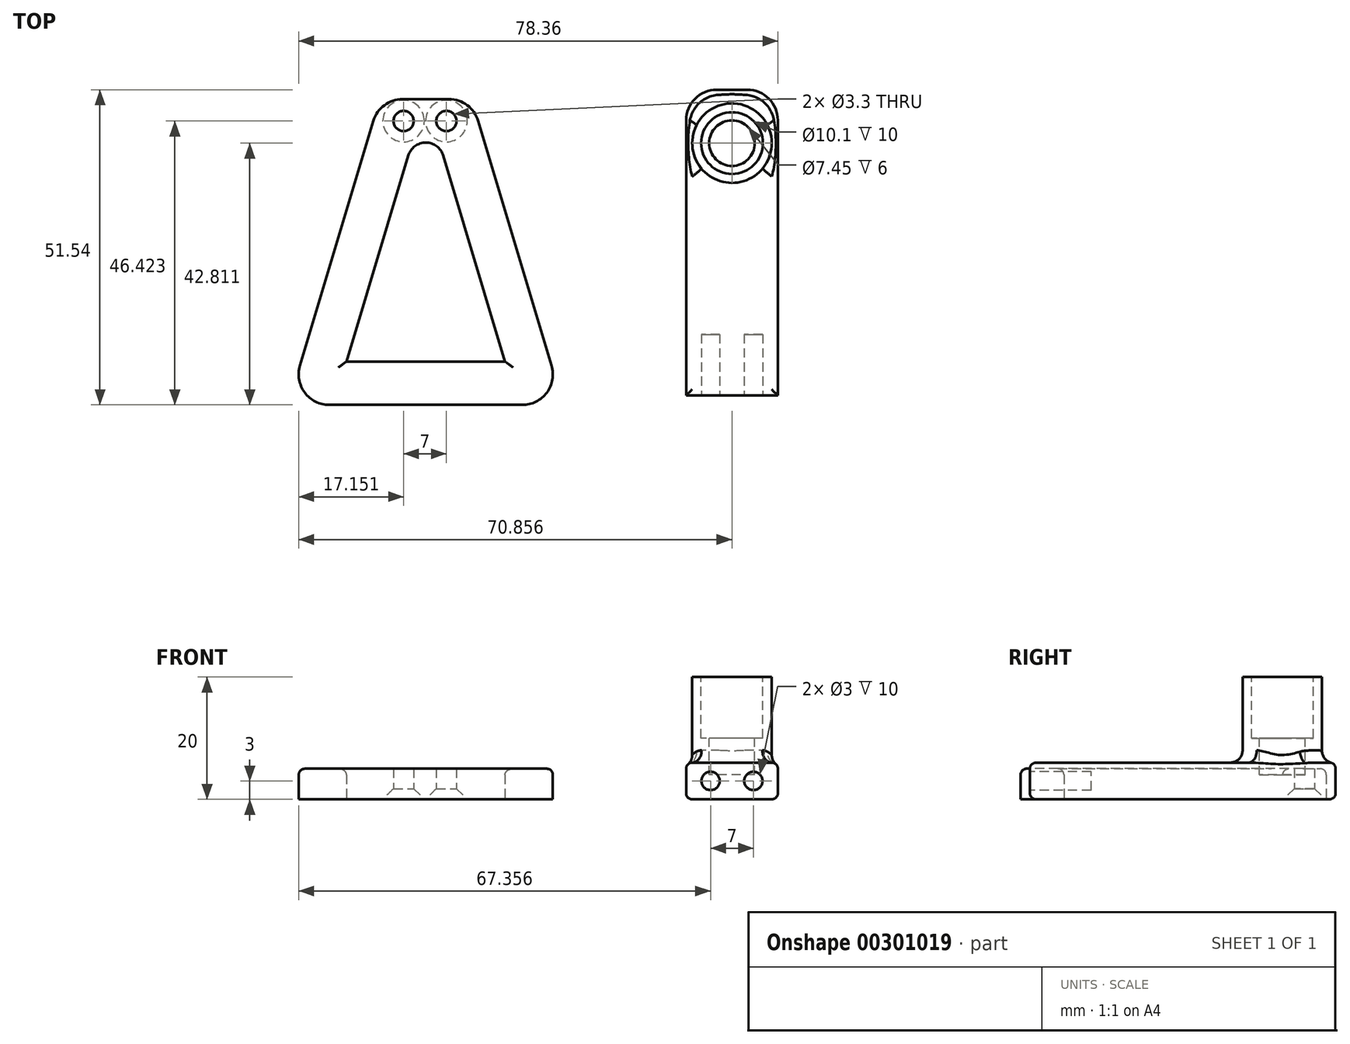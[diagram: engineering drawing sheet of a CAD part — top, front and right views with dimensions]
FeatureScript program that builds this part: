
annotation { "Feature Type Name" : "Feature", "Feature Type Description" : "" }
export const myFeature = defineFeature(function(context is Context, id is Id, definition is map)
    precondition{}
    {
        {
            var Q0;
            Q0=qCreatedBy(makeId("Top.planeOp"),FACE);
            var sketch = newSketch(context, id + "F0", { "sketchPlane" : qUnion([Q0])});
            skLineSegment(sketch, "E0.bottom", {"start": v(0, -1.54) * mm, "end": v(-45, -1.54) * mm});
            skLineSegment(sketch, "E0.top", {"start": v(-15, 48.46) * mm, "end": v(-30, 48.46) * mm});
            skLineSegment(sketch, "E1", {"start": v(-45, -1.54) * mm, "end": v(-30, 48.46) * mm});
            skLineSegment(sketch, "E2", {"start": v(-30, 48.46) * mm, "end": v(-15, 48.46) * mm});
            skLineSegment(sketch, "E3", {"start": v(-15, 48.46) * mm, "end": v(0, -1.54) * mm});
            skPoint(sketch, "E4.orphan", {"position": v(0, 48.46) * mm});
            skPoint(sketch, "E0.right.end.orphan", {"position": v(-45, 48.46) * mm});
            skLineSegment(sketch, "E5.0", {"start": v(-24.72, 41.36) * mm, "end": v(-20.28, 41.36) * mm});
            skLineSegment(sketch, "E5.1", {"start": v(-35.46, 5.56) * mm, "end": v(-24.72, 41.36) * mm});
            skLineSegment(sketch, "E5.2", {"start": v(-9.54, 5.56) * mm, "end": v(-35.46, 5.56) * mm});
            skLineSegment(sketch, "E5.3", {"start": v(-20.28, 41.36) * mm, "end": v(-9.54, 5.56) * mm});
            skSolve(sketch);
        }
        {
            var Q0;
            Q0=makeQuery(id+"F0.imprint","IMPRINT",FACE,{"disambiguationData":[TD([[makeQuery(id+"F0.imprint","IMPRINT",EDGE,{"derivedFrom":sQuery(id+"F0.wireOp",EDGE,"E0.bottom")}),-1.0]])]});
            extrude(context, id + "F1", {"entities" : qUnion([Q0]), "depth" : 5 * mm});
        }
        {
            var Q0;
            Q0=makeQuery(id+"F1.opExtrude","SWEPT_EDGE",EDGE,{"disambiguationData":[OSD([sQuery(id+"F0.wireOp",EDGE,"E0.bottom"),sQuery(id+"F0.wireOp",EDGE,"E1")])]});
            var Q1;
            Q1=makeQuery(id+"F1.opExtrude","SWEPT_EDGE",EDGE,{"disambiguationData":[OSD([sQuery(id+"F0.wireOp",EDGE,"E0.bottom"),sQuery(id+"F0.wireOp",EDGE,"E3")])]});
            var Q2;
            Q2=makeQuery(id+"F1.opExtrude","SWEPT_EDGE",EDGE,{"disambiguationData":[OSD([sQuery(id+"F0.wireOp",EDGE,"E2"),sQuery(id+"F0.wireOp",EDGE,"E3")])]});
            var Q3;
            Q3=makeQuery(id+"F1.opExtrude","SWEPT_EDGE",EDGE,{"disambiguationData":[OSD([sQuery(id+"F0.wireOp",EDGE,"E1"),sQuery(id+"F0.wireOp",EDGE,"E2")])]});
            fillet(context, id + "F2", {"entities" : qUnion([Q0, Q1, Q2, Q3]), "radius" : 5 * mm, "tangentPropagation" : true, "allowEdgeOverflow" : false});
        }
        {
            var Q0;
            Q0=makeQuery(id+"F1.opExtrude","CAP_FACE",FACE,{"disambiguationData":[OSD([sQuery(id+"F0.wireOp",EDGE,"E0.bottom"),sQuery(id+"F0.wireOp",EDGE,"E1"),sQuery(id+"F0.wireOp",EDGE,"E2"),sQuery(id+"F0.wireOp",EDGE,"E3"),sQuery(id+"F0.wireOp",EDGE,"E5.0"),sQuery(id+"F0.wireOp",EDGE,"E5.1"),sQuery(id+"F0.wireOp",EDGE,"E5.2"),sQuery(id+"F0.wireOp",EDGE,"E5.3")])],"isStart":true});
            var sketch = newSketch(context, id + "F3", { "sketchPlane" : qUnion([Q0])});
            skCircle(sketch, "E6", {"center": v(-26.13, -44.88) * mm, "radius": 1.5 * mm});
            skCircle(sketch, "E7", {"center": v(-19.13, -44.88) * mm, "radius": 1.5 * mm});
            skSolve(sketch);
        }
        {
            var Q0;
            Q0=sQuery(id+"F3.wireOp",VERTEX,"E7.center");
            var Q1;
            Q1=sQuery(id+"F3.wireOp",VERTEX,"E6.center");
            var Q2;
            Q2=makeQuery(id+"F1.opExtrude","SWEPT_BODY",BODY,{"disambiguationData":[OSD([sQuery(id+"F0.wireOp",EDGE,"E0.bottom"),sQuery(id+"F0.wireOp",EDGE,"E1"),sQuery(id+"F0.wireOp",EDGE,"E2"),sQuery(id+"F0.wireOp",EDGE,"E3"),sQuery(id+"F0.wireOp",EDGE,"E5.0"),sQuery(id+"F0.wireOp",EDGE,"E5.1"),sQuery(id+"F0.wireOp",EDGE,"E5.2"),sQuery(id+"F0.wireOp",EDGE,"E5.3")])]});
            hole(context, id + "F4", {"style" : HoleStyle.C_SINK, "endStyle" : HoleEndStyle.THROUGH, "holeDiameter" : 3.3 * mm, "cSinkDiameter" : 6.8 * mm, "cSinkAngle" : 90 * degree, "tappedDepth" : 12 * mm, "tapClearance" : 3, "locations" : qUnion([Q0, Q1]), "scope" : qUnion([Q2])});
        }
        {
            var Q0;
            Q0=makeQuery(id+"F1.opExtrude","SWEPT_EDGE",EDGE,{"disambiguationData":[OSD([sQuery(id+"F0.wireOp",EDGE,"E5.0"),sQuery(id+"F0.wireOp",EDGE,"E5.3")])]});
            var Q1;
            Q1=makeQuery(id+"F1.opExtrude","SWEPT_EDGE",EDGE,{"disambiguationData":[OSD([sQuery(id+"F0.wireOp",EDGE,"E5.0"),sQuery(id+"F0.wireOp",EDGE,"E5.1")])]});
            fillet(context, id + "F5", {"entities" : qUnion([Q0, Q1]), "radius" : 3 * mm, "tangentPropagation" : true, "allowEdgeOverflow" : false});
        }
        {
            var Q0;
            Q0=makeQuery(id+"F1.opExtrude","CAP_EDGE",EDGE,{"disambiguationData":[OSD([sQuery(id+"F0.wireOp",EDGE,"E5.3")])],"isStart":false});
            var Q1;
            Q1=makeQuery(id+"F1.opExtrude","CAP_EDGE",EDGE,{"disambiguationData":[OSD([sQuery(id+"F0.wireOp",EDGE,"E5.1")])],"isStart":false});
            var Q2;
            Q2=makeQuery(id+"F1.opExtrude","CAP_EDGE",EDGE,{"disambiguationData":[OSD([sQuery(id+"F0.wireOp",EDGE,"E5.2")])],"isStart":false});
            var Q3;
            Q3=makeQuery(id+"F1.opExtrude","CAP_EDGE",EDGE,{"disambiguationData":[OSD([sQuery(id+"F0.wireOp",EDGE,"E3")])],"isStart":false});
            fillet(context, id + "F6", {"entities" : qUnion([Q0, Q1, Q2, Q3]), "radius" : 1 * mm, "tangentPropagation" : true, "allowEdgeOverflow" : false});
        }
        {
            var Q0;
            Q0=qCreatedBy(makeId("Top.planeOp"),FACE);
            var sketch = newSketch(context, id + "F7", { "sketchPlane" : qUnion([Q0])});
            skLineSegment(sketch, "E8.bottom", {"start": v(20.08, 50) * mm, "end": v(35.08, 50) * mm});
            skLineSegment(sketch, "E8.top", {"start": v(20.08, 0) * mm, "end": v(35.08, 0) * mm});
            skLineSegment(sketch, "E8.left", {"start": v(20.08, 50) * mm, "end": v(20.08, 0) * mm});
            skLineSegment(sketch, "E8.right", {"start": v(35.08, 50) * mm, "end": v(35.08, 0) * mm});
            skSolve(sketch);
        }
        {
            var Q0;
            Q0 = qSketchRegion(id + "F7", true);
            extrude(context, id + "F8", {"entities" : qUnion([Q0]), "depth" : 6 * mm});
        }
        {
            var Q0;
            Q0=makeQuery(id+"F8.opExtrude","SWEPT_EDGE",EDGE,{"disambiguationData":[OSD([sQuery(id+"F7.wireOp",EDGE,"E8.bottom"),sQuery(id+"F7.wireOp",EDGE,"E8.left")])]});
            var Q1;
            Q1=makeQuery(id+"F8.opExtrude","SWEPT_EDGE",EDGE,{"disambiguationData":[OSD([sQuery(id+"F7.wireOp",EDGE,"E8.bottom"),sQuery(id+"F7.wireOp",EDGE,"E8.right")])]});
            fillet(context, id + "F9", {"entities" : qUnion([Q0, Q1]), "radius" : 5 * mm, "tangentPropagation" : true, "allowEdgeOverflow" : false});
        }
        {
            var Q0;
            Q0=makeQuery(id+"F8.opExtrude","CAP_FACE",FACE,{"disambiguationData":[OSD([sQuery(id+"F7.wireOp",EDGE,"E8.bottom"),sQuery(id+"F7.wireOp",EDGE,"E8.top"),sQuery(id+"F7.wireOp",EDGE,"E8.left"),sQuery(id+"F7.wireOp",EDGE,"E8.right")])],"isStart":false});
            var Q1;
            Q1=makeQuery(id+"F8.opExtrude","CAP_FACE",FACE,{"disambiguationData":[OSD([sQuery(id+"F7.wireOp",EDGE,"E8.bottom"),sQuery(id+"F7.wireOp",EDGE,"E8.top"),sQuery(id+"F7.wireOp",EDGE,"E8.left"),sQuery(id+"F7.wireOp",EDGE,"E8.right")])],"isStart":true});
            fillet(context, id + "F10", {"entities" : qUnion([Q0, Q1]), "radius" : 1 * mm, "tangentPropagation" : true, "allowEdgeOverflow" : false});
        }
        {
            var Q0;
            Q0=makeQuery(id+"F8.opExtrude","CAP_FACE",FACE,{"disambiguationData":[OSD([sQuery(id+"F7.wireOp",EDGE,"E8.bottom"),sQuery(id+"F7.wireOp",EDGE,"E8.top"),sQuery(id+"F7.wireOp",EDGE,"E8.left"),sQuery(id+"F7.wireOp",EDGE,"E8.right")])],"isStart":false});
            var sketch = newSketch(context, id + "F11", { "sketchPlane" : qUnion([Q0])});
            skCircle(sketch, "E9", {"center": v(27.58, 41.27) * mm, "radius": 6.5 * mm});
            skPoint(sketch, "E9.centerSnap0", {"position": v(27.58, 49) * mm});
            skSolve(sketch);
        }
        {
            var Q0;
            Q0 = qSketchRegion(id + "F11", true);
            extrude(context, id + "F12", {"entities" : qUnion([Q0]), "operationType" : NewBodyOperationType.ADD, "depth" : 14 * mm});
        }
        {
            var Q0;
            Q0=makeQuery(id+"F12.opExtrude","CAP_EDGE",EDGE,{"disambiguationData":[OSD([sQuery(id+"F11.wireOp",EDGE,"E9")])],"isStart":true});
            fillet(context, id + "F13", {"entities" : qUnion([Q0]), "radius" : 2 * mm, "tangentPropagation" : true, "allowEdgeOverflow" : false});
        }
        {
            var Q0;
            Q0=makeQuery(id+"F12.opExtrude","CAP_FACE",FACE,{"disambiguationData":[OSD([sQuery(id+"F11.wireOp",EDGE,"E9")])],"isStart":false});
            var sketch = newSketch(context, id + "F14", { "sketchPlane" : qUnion([Q0])});
            skCircle(sketch, "E10", {"center": v(27.58, 41.27) * mm, "radius": 5.05 * mm});
            skSolve(sketch);
        }
        {
            var Q0;
            Q0=makeQuery(id+"F14.imprint","IMPRINT",FACE,{"disambiguationData":[TD([[makeQuery(id+"F14.imprint","IMPRINT",EDGE,{"derivedFrom":sQuery(id+"F14.wireOp",EDGE,"E10")}),1.0]])]});
            extrude(context, id + "F15", {"entities" : qUnion([Q0]), "operationType" : NewBodyOperationType.REMOVE, "oppositeDirection" : true, "depth" : 10 * mm});
        }
        {
            var Q0;
            Q0=makeQuery(id+"F15.boolean.opBoolean","COPY",FACE,{"derivedFrom":makeQuery(id+"F15.opExtrude","CAP_FACE",FACE,{"disambiguationData":[OSD([sQuery(id+"F14.wireOp",EDGE,"E10")])],"isStart":false})});
            var sketch = newSketch(context, id + "F16", { "sketchPlane" : qUnion([Q0])});
            skCircle(sketch, "E11", {"center": v(27.58, 41.27) * mm, "radius": 3.72 * mm});
            skSolve(sketch);
        }
        {
            var Q0;
            Q0 = qSketchRegion(id + "F16", true);
            extrude(context, id + "F17", {"entities" : qUnion([Q0]), "operationType" : NewBodyOperationType.REMOVE, "oppositeDirection" : true, "depth" : 6 * mm});
        }
        {
            var Q0;
            Q0=makeQuery(id+"F8.opExtrude","SWEPT_FACE",FACE,{"disambiguationData":[OSD([sQuery(id+"F7.wireOp",EDGE,"E8.top")])]});
            var sketch = newSketch(context, id + "F18", { "sketchPlane" : qUnion([Q0])});
            skCircle(sketch, "E12", {"center": v(24.08, 3) * mm, "radius": 1.5 * mm});
            skPoint(sketch, "E12.centerSnap0", {"position": v(20.08, 3) * mm});
            skCircle(sketch, "E13", {"center": v(31.08, 3) * mm, "radius": 1.5 * mm});
            skSolve(sketch);
        }
        {
            var Q0;
            Q0=makeQuery(id+"F18.imprint","IMPRINT",FACE,{"disambiguationData":[TD([[makeQuery(id+"F18.imprint","IMPRINT",EDGE,{"derivedFrom":sQuery(id+"F18.wireOp",EDGE,"E12")}),1.0]])]});
            var Q1;
            Q1=makeQuery(id+"F18.imprint","IMPRINT",FACE,{"disambiguationData":[TD([[makeQuery(id+"F18.imprint","IMPRINT",EDGE,{"derivedFrom":sQuery(id+"F18.wireOp",EDGE,"E13")}),1.0]])]});
            extrude(context, id + "F19", {"entities" : qUnion([Q0, Q1]), "operationType" : NewBodyOperationType.REMOVE, "oppositeDirection" : true, "depth" : 10 * mm});
        }
    });
